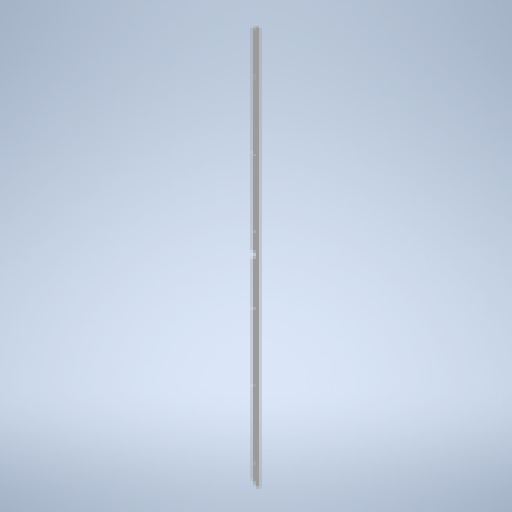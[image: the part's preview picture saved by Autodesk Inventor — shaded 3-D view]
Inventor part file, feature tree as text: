
AUTODESK INVENTOR PART (.ipt)
format: ipt  version: 2025 (Build 290162010, 162A)  size: 893,952 bytes
history: native  units: mm
features: other x5, sketch x4, extrude x2, pattern_linear x2, projected_geometry x2, sheet_metal_op x1
ambient origin geometry x8: Origin, YZ Plane, XZ Plane, XY Plane, X Axis, Y Axis, Z Axis, Center Point
bodies: Body1 (feature_tree)
feature tree (16):
  sheet_metal_op  "Face2"
  extrude  "Extrusion2"  Depth=2980.0mm
  pattern_linear  "Rectangular Pattern1"  Spacing1=142.0mm  [1 undecoded]
  extrude  "Extrusion3"  TaperAngle=0.0deg  [1 undecoded]
  pattern_linear  "Rectangular Pattern2"  Count1=6  [1 undecoded]
  other  "Corner Chamfer1"
  other  "Corner Chamfer2"
  other  "Mark2"
  sketch  "Sketch6"  dims[d26=60.107271mm d27=2980.0mm]
  other  "Plate4"
  sketch  "Sketch7"  dims[d28=3.0mm]
  projected_geometry  "Projected Loop1"
  sketch  "Sketch8"  dims[d29=31.053636mm]
  projected_geometry  "Projected Loop2"
  sketch  "Sketch10"  dims[d30=3.2mm d31=142.0mm d32=0.0mm d33=0.0mm d34=60.0mm d36=500.0mm d37=50.0mm d38=1490.0mm d39=0.0mm d40=0.0mm d41=30.0mm d43=1480.0mm d48=6.0mm d49=6.0mm d50=45.0deg d51=6.0mm d52=6.0mm d53=45.0deg d54=200.0mm d55=15.0mm]
  other  "Definition1"
note: 3 required parameter values undecoded (feature->parameter linkage not recoverable at this tier; creation-order binding heuristic only, values carry confidence <= 0.55)
